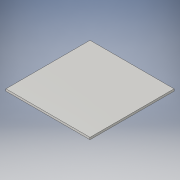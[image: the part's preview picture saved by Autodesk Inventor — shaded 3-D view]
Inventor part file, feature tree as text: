
AUTODESK INVENTOR PART (.ipt)
format: ipt  version: 2016 (Build 200138000, 138)  size: 87,552 bytes
history: native  units: in
note: dims shown in document units (in); Inventor stores cm internally (conversion verified against a paired STEP export)
features: extrude x1, sketch x1
ambient origin geometry x8: Origin, YZ Plane, XZ Plane, XY Plane, X Axis, Y Axis, Z Axis, Center Point
bodies: Solid1 (feature_tree)
feature tree (2):
  extrude  "Extrusion1"  Depth=10.0in
  sketch  "Sketch1"  dims[d0=10.0in d1=10.0in d2=0.25in d3=0.0in]
